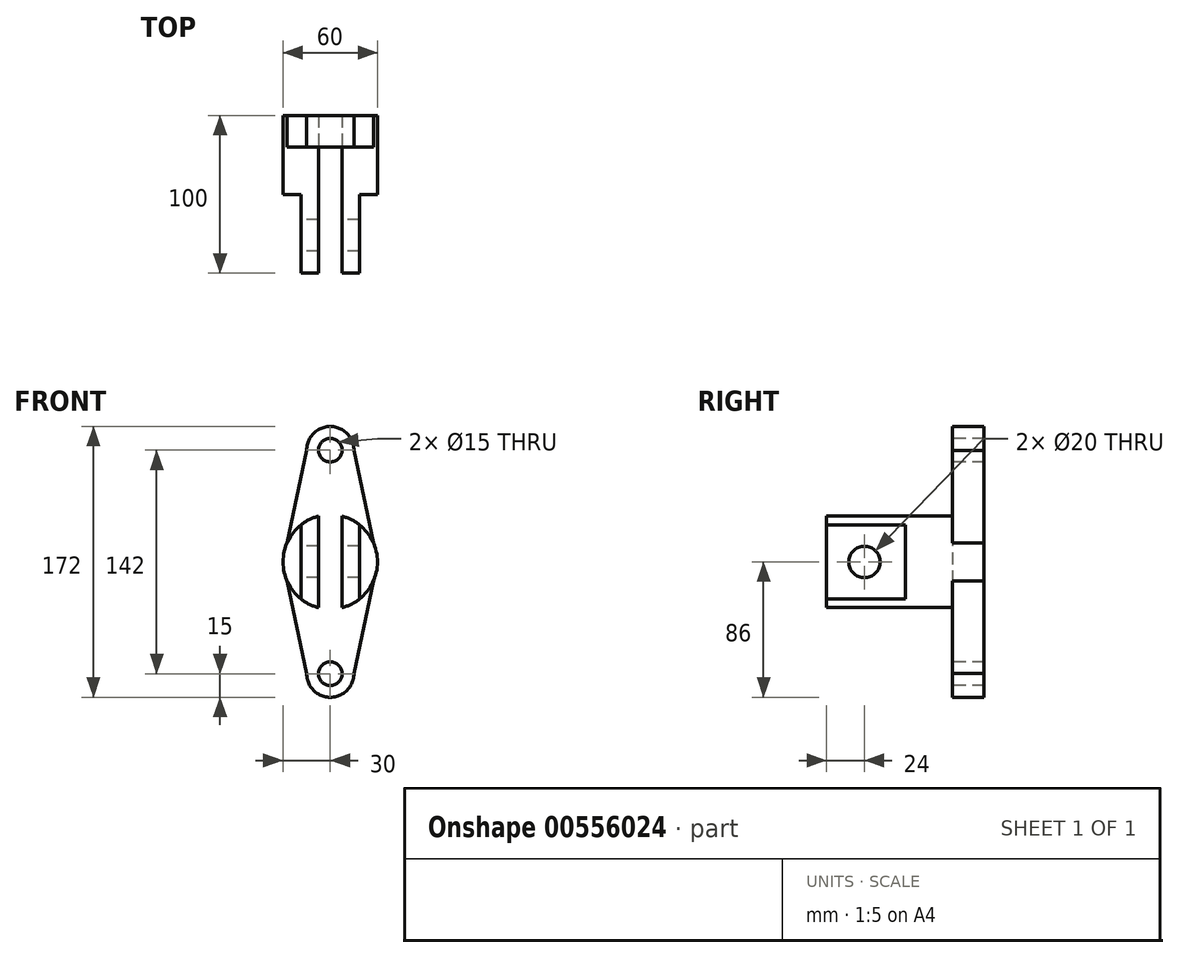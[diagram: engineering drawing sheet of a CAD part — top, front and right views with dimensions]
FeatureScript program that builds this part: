
annotation { "Feature Type Name" : "Feature", "Feature Type Description" : "" }
export const myFeature = defineFeature(function(context is Context, id is Id, definition is map)
    precondition{}
    {
        {
            var Q0;
            Q0=qCreatedBy(makeId("Front.planeOp"),FACE);
            var sketch = newSketch(context, id + "F0", { "sketchPlane" : qUnion([Q0])});
            skArc(sketch, "E0", {"start": v(15, 70.86) * mm, "mid": v(0, 86) * mm, "end": v(-15, 70.86) * mm});
            skArc(sketch, "E1", {"start": v(-15, -70.86) * mm, "mid": v(0, -86) * mm, "end": v(15, -70.86) * mm});
            skArc(sketch, "E2", {"start": v(-27.43, 12.16) * mm, "mid": v(-30, 0) * mm, "end": v(-27.43, -12.16) * mm});
            skLineSegment(sketch, "E3", {"start": v(-15, 70.86) * mm, "end": v(-27.43, 12.16) * mm});
            skLineSegment(sketch, "E4", {"start": v(-27.43, -12.16) * mm, "end": v(-15, -70.86) * mm});
            skLineSegment(sketch, "E5", {"start": v(15, -70.86) * mm, "end": v(27.43, -12.16) * mm});
            skLineSegment(sketch, "E6", {"start": v(27.43, 12.16) * mm, "end": v(15, 70.86) * mm});
            skPoint(sketch, "E7.orphan", {"position": v(-30, 0) * mm});
            skPoint(sketch, "E8.orphan", {"position": v(30, 0) * mm});
            skArc(sketch, "E9.trimOffspring", {"start": v(27.43, -12.16) * mm, "mid": v(30, 0) * mm, "end": v(27.43, 12.16) * mm});
            skSolve(sketch);
        }
        {
            var Q0;
            Q0 = qSketchRegion(id + "F0", true);
            extrude(context, id + "F1", {"entities" : qUnion([Q0]), "depth" : 20 * mm, "offsetDistance" : 25 * mm});
        }
        {
            var Q0;
            Q0=makeQuery(id+"F1.opExtrude","CAP_FACE",FACE,{"disambiguationData":[OSD([sQuery(id+"F0.wireOp",EDGE,"E0"),sQuery(id+"F0.wireOp",EDGE,"E1"),sQuery(id+"F0.wireOp",EDGE,"E2"),sQuery(id+"F0.wireOp",EDGE,"E3"),sQuery(id+"F0.wireOp",EDGE,"E4"),sQuery(id+"F0.wireOp",EDGE,"E5"),sQuery(id+"F0.wireOp",EDGE,"E6"),sQuery(id+"F0.wireOp",EDGE,"E9.trimOffspring")])],"isStart":false});
            var sketch = newSketch(context, id + "F2", { "sketchPlane" : qUnion([Q0])});
            skArc(sketch, "E10", {"start": v(-7.5, 29.05) * mm, "mid": v(-30, 0) * mm, "end": v(-7.5, -29.05) * mm});
            skLineSegment(sketch, "E11.left", {"start": v(7.5, 29.05) * mm, "end": v(7.5, -29.05) * mm});
            skLineSegment(sketch, "E11.right", {"start": v(-7.5, 29.05) * mm, "end": v(-7.5, -29.05) * mm});
            skArc(sketch, "E12.trimOffspring", {"start": v(7.5, -29.05) * mm, "mid": v(30, 0) * mm, "end": v(7.5, 29.05) * mm});
            skSolve(sketch);
        }
        {
            var Q0;
            {var subQ2=sQuery(id+"F2.wireOp",EDGE,"E11.right");Q0=makeQuery(id+"F2.imprint","IMPRINT",FACE,{"disambiguationData":[TD([[makeQuery(id+"F2.imprint","IMPRINT",EDGE,{"derivedFrom":subQ2}),-1.0]])]});}
            var Q1;
            {var subQ0=sQuery(id+"F2.wireOp",EDGE,"E11.left");Q1=makeQuery(id+"F2.imprint","IMPRINT",FACE,{"disambiguationData":[TD([[makeQuery(id+"F2.imprint","IMPRINT",EDGE,{"derivedFrom":subQ0}),1.0]])]});}
            extrude(context, id + "F3", {"entities" : qUnion([Q0, Q1]), "operationType" : NewBodyOperationType.ADD, "depth" : 30 * mm, "offsetDistance" : 25 * mm});
        }
        {
            var Q0;
            Q0=makeQuery(id+"F3.opExtrude","CAP_FACE",FACE,{"disambiguationData":[OSD([sQuery(id+"F2.wireOp",EDGE,"E10"),sQuery(id+"F2.wireOp",EDGE,"E11.right")])],"isStart":false});
            var sketch = newSketch(context, id + "F4", { "sketchPlane" : qUnion([Q0])});
            skArc(sketch, "E13", {"start": v(-7.5, 29.05) * mm, "mid": v(-13.28, 26.9) * mm, "end": v(-18.5, 23.62) * mm});
            skLineSegment(sketch, "E14.left", {"start": v(18.5, 23.62) * mm, "end": v(18.5, -23.62) * mm});
            skLineSegment(sketch, "E14.right", {"start": v(-18.5, 23.62) * mm, "end": v(-18.5, -23.62) * mm});
            skLineSegment(sketch, "E15.left", {"start": v(7.5, 29.05) * mm, "end": v(7.5, -29.05) * mm});
            skLineSegment(sketch, "E15.right", {"start": v(-7.5, 29.05) * mm, "end": v(-7.5, -29.05) * mm});
            skArc(sketch, "E16.trimOffspring", {"start": v(-18.5, -23.62) * mm, "mid": v(-13.28, -26.9) * mm, "end": v(-7.5, -29.05) * mm});
            skArc(sketch, "E17.trimOffspring", {"start": v(7.5, -29.05) * mm, "mid": v(13.28, -26.9) * mm, "end": v(18.5, -23.62) * mm});
            skArc(sketch, "E18.trimOffspring", {"start": v(18.5, 23.62) * mm, "mid": v(13.28, 26.9) * mm, "end": v(7.5, 29.05) * mm});
            skSolve(sketch);
        }
        {
            var Q0;
            Q0=makeQuery(id+"F4.imprint","IMPRINT",FACE,{"disambiguationData":[TD([[makeQuery(id+"F4.imprint","IMPRINT",EDGE,{"derivedFrom":sQuery(id+"F4.wireOp",EDGE,"E14.left")}),-1.0]])]});
            var Q1;
            Q1=makeQuery(id+"F4.imprint","IMPRINT",FACE,{"disambiguationData":[TD([[makeQuery(id+"F4.imprint","IMPRINT",EDGE,{"derivedFrom":sQuery(id+"F4.wireOp",EDGE,"E13")}),1.0]])]});
            extrude(context, id + "F5", {"entities" : qUnion([Q0, Q1]), "operationType" : NewBodyOperationType.ADD, "depth" : 50 * mm, "offsetDistance" : 25 * mm});
        }
        {
            var Q0;
            Q0=makeQuery(id+"F5.opExtrude","SWEPT_FACE",FACE,{"disambiguationData":[OSD([sQuery(id+"F4.wireOp",EDGE,"E14.right")])]});
            var sketch = newSketch(context, id + "F6", { "sketchPlane" : qUnion([Q0])});
            skPoint(sketch, "E19", {"position": v(76, 0) * mm});
            skSolve(sketch);
        }
        {
            var Q0;
            Q0=makeQuery(id+"F1.opExtrude","CAP_FACE",FACE,{"disambiguationData":[OSD([sQuery(id+"F0.wireOp",EDGE,"E0"),sQuery(id+"F0.wireOp",EDGE,"E1"),sQuery(id+"F0.wireOp",EDGE,"E2"),sQuery(id+"F0.wireOp",EDGE,"E3"),sQuery(id+"F0.wireOp",EDGE,"E4"),sQuery(id+"F0.wireOp",EDGE,"E5"),sQuery(id+"F0.wireOp",EDGE,"E6"),sQuery(id+"F0.wireOp",EDGE,"E9.trimOffspring")])],"isStart":false});
            var sketch = newSketch(context, id + "F7", { "sketchPlane" : qUnion([Q0])});
            skPoint(sketch, "E20", {"position": v(0, 71) * mm});
            skPoint(sketch, "E21", {"position": v(0, -71) * mm});
            skSolve(sketch);
        }
        {
            var Q0;
            Q0=sQuery(id+"F6.wireOp",VERTEX,"E19");
            var Q1;
            Q1=makeQuery(id+"F1.opExtrude","SWEPT_BODY",BODY,{"disambiguationData":[OSD([sQuery(id+"F0.wireOp",EDGE,"E0"),sQuery(id+"F0.wireOp",EDGE,"E1"),sQuery(id+"F0.wireOp",EDGE,"E2"),sQuery(id+"F0.wireOp",EDGE,"E3"),sQuery(id+"F0.wireOp",EDGE,"E4"),sQuery(id+"F0.wireOp",EDGE,"E5"),sQuery(id+"F0.wireOp",EDGE,"E6"),sQuery(id+"F0.wireOp",EDGE,"E9.trimOffspring")])]});
            hole(context, id + "F8", {"style" : HoleStyle.SIMPLE, "endStyle" : HoleEndStyle.THROUGH, "holeDiameter" : 20 * mm, "isTappedThrough" : true, "tappedDepth" : 12 * mm, "tapClearance" : 3, "locations" : qUnion([Q0]), "scope" : qUnion([Q1])});
        }
        {
            var Q0;
            Q0=sQuery(id+"F7.wireOp",VERTEX,"E20");
            var Q1;
            Q1=sQuery(id+"F7.wireOp",VERTEX,"E21");
            var Q2;
            Q2=makeQuery(id+"F1.opExtrude","SWEPT_BODY",BODY,{"disambiguationData":[OSD([sQuery(id+"F0.wireOp",EDGE,"E0"),sQuery(id+"F0.wireOp",EDGE,"E1"),sQuery(id+"F0.wireOp",EDGE,"E2"),sQuery(id+"F0.wireOp",EDGE,"E3"),sQuery(id+"F0.wireOp",EDGE,"E4"),sQuery(id+"F0.wireOp",EDGE,"E5"),sQuery(id+"F0.wireOp",EDGE,"E6"),sQuery(id+"F0.wireOp",EDGE,"E9.trimOffspring")])]});
            hole(context, id + "F9", {"style" : HoleStyle.SIMPLE, "endStyle" : HoleEndStyle.THROUGH, "holeDiameter" : 15 * mm, "isTappedThrough" : true, "tappedDepth" : 12 * mm, "tapClearance" : 3, "locations" : qUnion([Q0, Q1]), "scope" : qUnion([Q2])});
        }
    });
